# Revit family: 18497-presto
name_source: partatom
category: Plumbing Fixtures
units: mm (PartAtom-declared; Revit-internal decimal feet)

## family parameters
Always vertical = Yes
Cut with Voids When Loaded = No
Maintain Annotation Orientation = No
OmniClass Number = 23.45.00.00
OmniClass Title = Sanitary, Laundry, and Cleaning Equipment
Part Type = Normal
Room Calculation Point = No
Round Connector Dimension = Use Diameter
Shared = No
Work Plane-Based = No

## types (1)
- 18497-presto
    - Hydraulic supply = 25.00 mm
    -Delivered with = 6 galvanized anchor pins, M8 supplied / - 2 brackets for wall fixing, lenght: 180 mm, supplied with screw: 6.3X45 and wall dowel (nylon D8)
    > Standards & approvals = Molded chrome-plated body in accordance with EN 12540 / - 200-hour neutral salt spray resistant (NSS) in accordance with ISO 9227
    Assembly Code = 18497
    Default Elevation = 0 mm  [stored 0 ft]
    Description = Support frame without tap for SENSAO 8100N/8300N/8500N/8600N
    Model = 18497
    Recommended pressure = 3.0 bar
    Technical Sheet = https://www.prestodatashare.com
    URL = https://www.prestodatashare.com
    brand = LES ROBINETS PRESTO
    flow = 6.0 L/s
    flow time = 1.0 s
    min flow = 1.0 L/s
    min pressure = 1.0 bar
    power = 0 W
    pressure = 5.0 bar
    range = Ready-to-install self-supporting mounting frame for urinal

note: [stored X ft] marks values corroborated as IEEE doubles in the binary element streams (Revit-internal decimal feet)

## geometry (parser evidence)
native form markers: Sweep x3
no freeform markers — native parametric forms only
